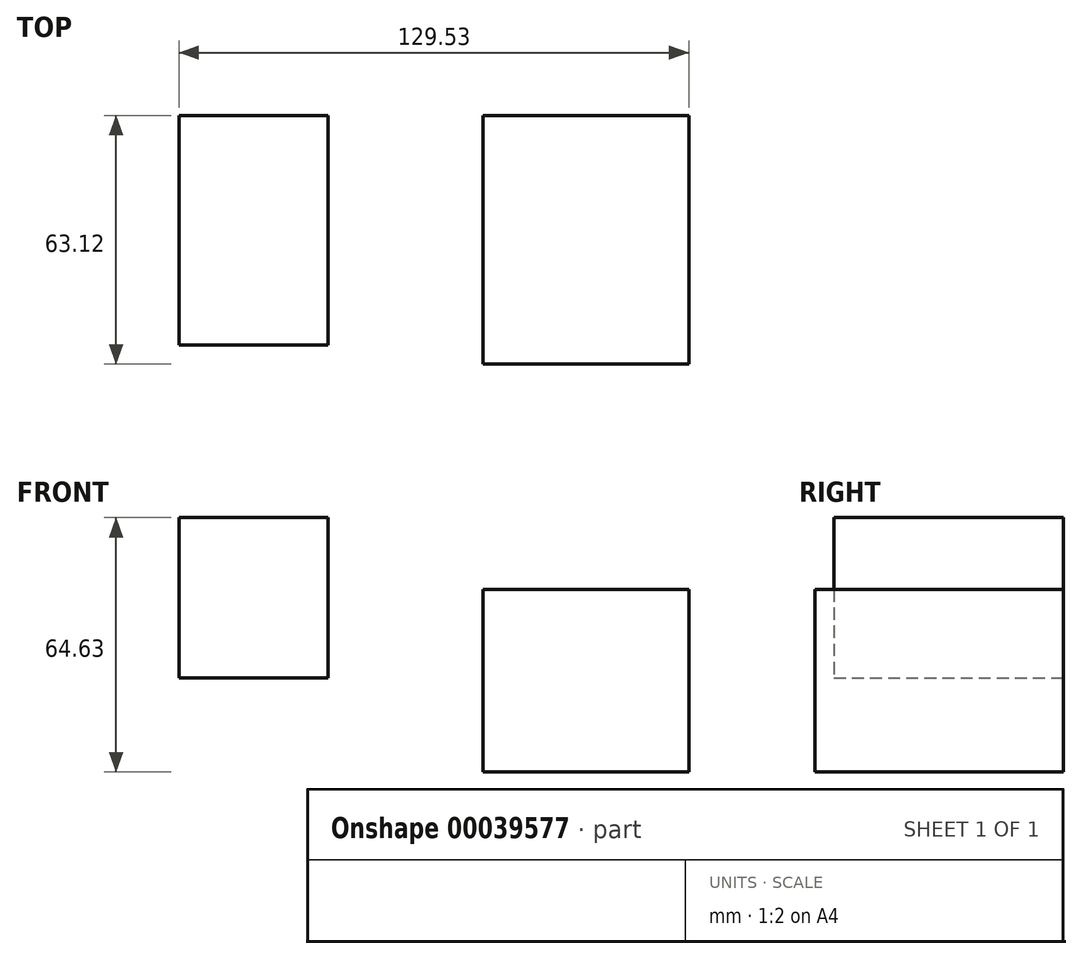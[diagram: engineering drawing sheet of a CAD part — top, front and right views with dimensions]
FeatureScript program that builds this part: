
annotation { "Feature Type Name" : "Feature", "Feature Type Description" : "" }
export const myFeature = defineFeature(function(context is Context, id is Id, definition is map)
    precondition{}
    {
        {
            var Q0;
            Q0=qCreatedBy(makeId("Front.planeOp"),FACE);
            var sketch = newSketch(context, id + "F0", { "sketchPlane" : qUnion([Q0])});
            skLineSegment(sketch, "E0.rect.bottom", {"start": v(-101.92, 30.72) * mm, "end": v(-139.81, 30.72) * mm});
            skLineSegment(sketch, "E0.rect.top", {"start": v(-101.92, -10.07) * mm, "end": v(-139.81, -10.07) * mm});
            skLineSegment(sketch, "E0.rect.left", {"start": v(-101.92, 30.72) * mm, "end": v(-101.92, -10.07) * mm});
            skLineSegment(sketch, "E0.rect.right", {"start": v(-139.81, 30.72) * mm, "end": v(-139.81, -10.07) * mm});
            skPoint(sketch, "E0.rect.middle", {"position": v(-120.86, 10.33) * mm});
            skSolve(sketch);
        }
        {
            var Q0;
            Q0 = qSketchRegion(id + "F0", true);
            extrude(context, id + "F1", {"entities" : qUnion([Q0]), "depth" : 58.26 * mm});
        }
        {
            var Q0;
            Q0=makeQuery(id+"F1.opExtrude","SWEPT_BODY",BODY,{"disambiguationData":[OSD([sQuery(id+"F0.wireOp",EDGE,"E0.rect.bottom"),sQuery(id+"F0.wireOp",EDGE,"E0.rect.top"),sQuery(id+"F0.wireOp",EDGE,"E0.rect.left"),sQuery(id+"F0.wireOp",EDGE,"E0.rect.right")])]});
            transform(context, id + "F2", {"entities" : qUnion([Q0]), "transformType" : TransformType.TRANSLATION_3D, "dx" : 89.23 * mm, "dy" : 0 * mm, "dz" : 0 * mm, "makeCopy" : true});
        }
        {
            var Q0;
            Q0=makeQuery(id+"F1.opExtrude","SWEPT_BODY",BODY,{"disambiguationData":[OSD([sQuery(id+"F0.wireOp",EDGE,"E0.rect.bottom"),sQuery(id+"F0.wireOp",EDGE,"E0.rect.top"),sQuery(id+"F0.wireOp",EDGE,"E0.rect.left"),sQuery(id+"F0.wireOp",EDGE,"E0.rect.right")])]});
            deleteBodies(context, id + "F3", {"entities" : qUnion([Q0])});
        }
        {
            var Q0;
            Q0=qCreatedBy(makeId("Front.planeOp"),FACE);
            var sketch = newSketch(context, id + "F4", { "sketchPlane" : qUnion([Q0])});
            skLineSegment(sketch, "E1.rect.bottom", {"start": v(26.7, 12.44) * mm, "end": v(78.95, 12.44) * mm});
            skLineSegment(sketch, "E1.rect.top", {"start": v(26.7, -33.9) * mm, "end": v(78.95, -33.9) * mm});
            skLineSegment(sketch, "E1.rect.left", {"start": v(26.7, 12.44) * mm, "end": v(26.7, -33.9) * mm});
            skLineSegment(sketch, "E1.rect.right", {"start": v(78.95, 12.44) * mm, "end": v(78.95, -33.9) * mm});
            skPoint(sketch, "E1.rect.middle", {"position": v(52.82, -10.73) * mm});
            skSolve(sketch);
        }
        {
            var Q0;
            Q0=makeQuery(id+"F4.imprint","IMPRINT",FACE,{"disambiguationData":[TD([[makeQuery(id+"F4.imprint","IMPRINT",EDGE,{"derivedFrom":sQuery(id+"F4.wireOp",EDGE,"E1.rect.bottom")}),-1.0]])]});
            extrude(context, id + "F5", {"entities" : qUnion([Q0]), "depth" : 63.12 * mm});
        }
    });
